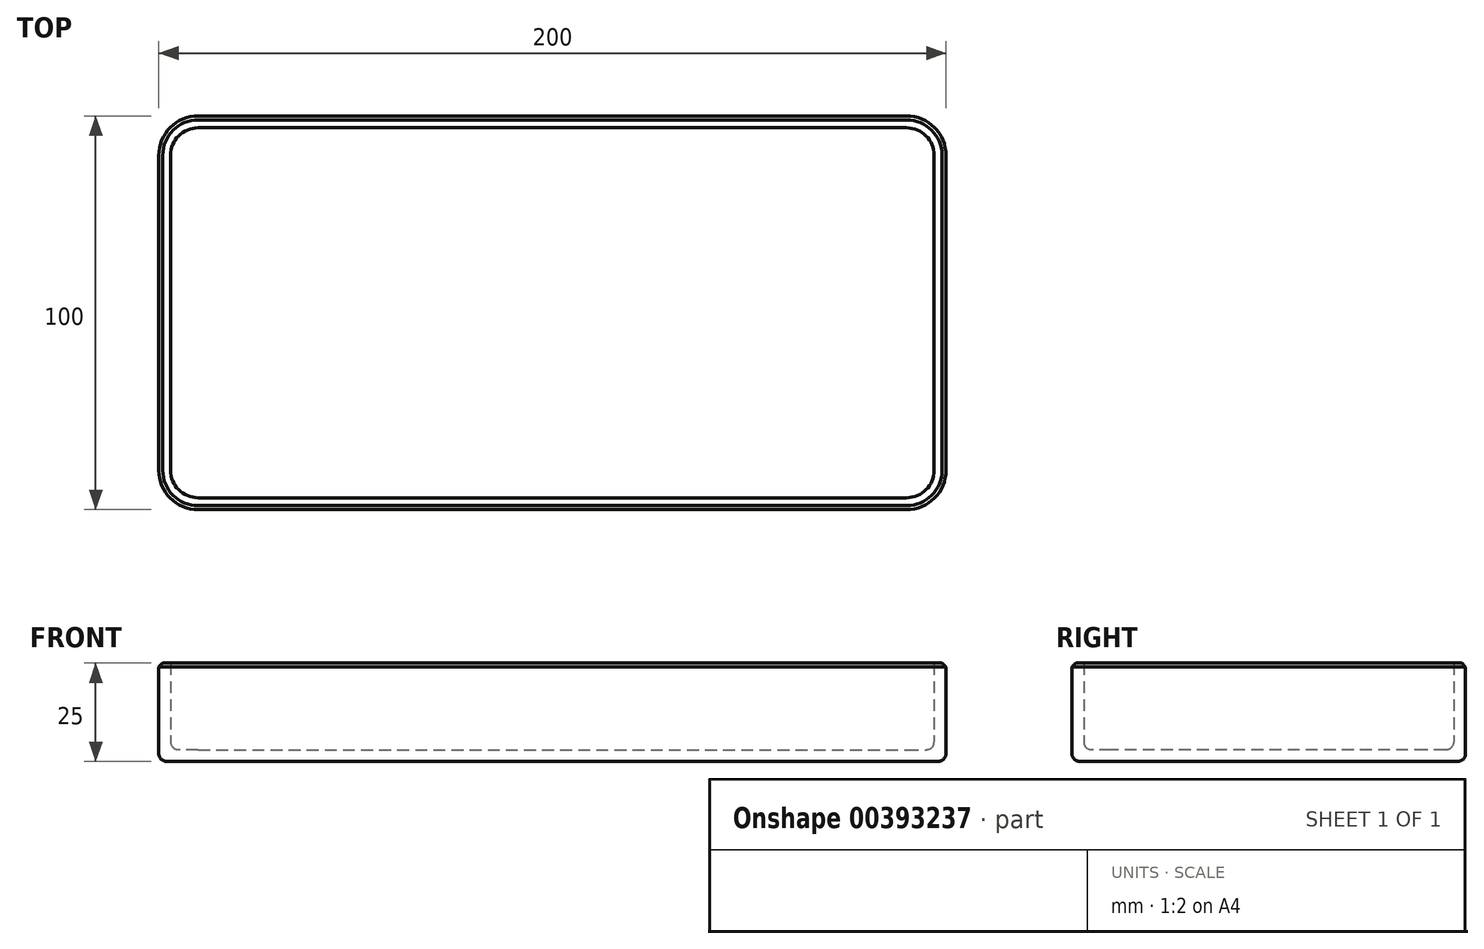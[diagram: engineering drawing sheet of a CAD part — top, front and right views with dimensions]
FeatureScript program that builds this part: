
annotation { "Feature Type Name" : "Feature", "Feature Type Description" : "" }
export const myFeature = defineFeature(function(context is Context, id is Id, definition is map)
    precondition{}
    {
        {
            var Q0;
            Q0=qCreatedBy(makeId("Top.planeOp"),FACE);
            var sketch = newSketch(context, id + "F0", { "sketchPlane" : qUnion([Q0])});
            skLineSegment(sketch, "E0.bottom", {"start": v(0.74, 0) * mm, "end": v(180.74, 0) * mm});
            skLineSegment(sketch, "E0.top", {"start": v(0.74, -100) * mm, "end": v(180.74, -100) * mm});
            skLineSegment(sketch, "E0.left", {"start": v(-9.26, -10) * mm, "end": v(-9.26, -90) * mm});
            skLineSegment(sketch, "E0.right", {"start": v(190.74, -10) * mm, "end": v(190.74, -90) * mm});
            skPoint(sketch, "E0.middle", {"position": v(90.74, -50) * mm});
            skPoint(sketch, "E1.visualSharp", {"position": v(-9.26, 0) * mm});
            skArc(sketch, "E1.filletArc", {"start": v(0.74, 0) * mm, "mid": v(-6.33, -2.93) * mm, "end": v(-9.26, -10) * mm});
            skPoint(sketch, "E2.visualSharp", {"position": v(-9.26, -100) * mm});
            skArc(sketch, "E2.filletArc", {"start": v(-9.26, -90) * mm, "mid": v(-6.33, -97.07) * mm, "end": v(0.74, -100) * mm});
            skPoint(sketch, "E3.visualSharp", {"position": v(190.74, -100) * mm});
            skArc(sketch, "E3.filletArc", {"start": v(180.74, -100) * mm, "mid": v(187.8, -97.07) * mm, "end": v(190.74, -90) * mm});
            skPoint(sketch, "E4.visualSharp", {"position": v(190.74, 0) * mm});
            skArc(sketch, "E4.filletArc", {"start": v(190.74, -10) * mm, "mid": v(187.8, -2.93) * mm, "end": v(180.74, 0) * mm});
            skLineSegment(sketch, "E5.0", {"start": v(0.74, -3) * mm, "end": v(180.74, -3) * mm});
            skArc(sketch, "E5.1", {"start": v(187.74, -10) * mm, "mid": v(185.69, -5.05) * mm, "end": v(180.74, -3) * mm});
            skArc(sketch, "E5.2", {"start": v(0.74, -3) * mm, "mid": v(-4.21, -5.05) * mm, "end": v(-6.26, -10) * mm});
            skLineSegment(sketch, "E5.3", {"start": v(187.74, -10) * mm, "end": v(187.74, -90) * mm});
            skLineSegment(sketch, "E5.4", {"start": v(-6.26, -10) * mm, "end": v(-6.26, -90) * mm});
            skArc(sketch, "E5.5", {"start": v(-6.26, -90) * mm, "mid": v(-4.21, -94.95) * mm, "end": v(0.74, -97) * mm});
            skLineSegment(sketch, "E5.6", {"start": v(0.74, -97) * mm, "end": v(180.74, -97) * mm});
            skArc(sketch, "E5.7", {"start": v(180.74, -97) * mm, "mid": v(185.69, -94.95) * mm, "end": v(187.74, -90) * mm});
            skSolve(sketch);
        }
        {
            var Q0;
            Q0=makeQuery(id+"F0.imprint","IMPRINT",FACE,{"disambiguationData":[TD([[makeQuery(id+"F0.imprint","IMPRINT",EDGE,{"derivedFrom":sQuery(id+"F0.wireOp",EDGE,"E0.bottom")}),-1.0]])]});
            extrude(context, id + "F1", {"entities" : qUnion([Q0]), "depth" : 25 * mm});
        }
        {
            var Q0;
            Q0=makeQuery(id+"F0.imprint","IMPRINT",FACE,{"disambiguationData":[TD([[makeQuery(id+"F0.imprint","IMPRINT",EDGE,{"derivedFrom":sQuery(id+"F0.wireOp",EDGE,"E5.0")}),-1.0]])]});
            extrude(context, id + "F2", {"entities" : qUnion([Q0]), "operationType" : NewBodyOperationType.ADD, "depth" : 3 * mm});
        }
        {
            var Q0;
            Q0=makeQuery(id+"F2.opExtrude","CAP_EDGE",EDGE,{"disambiguationData":[OSD([sQuery(id+"F0.wireOp",EDGE,"E5.4")])],"isStart":false});
            var Q1;
            Q1=makeQuery(id+"F2.opExtrude","CAP_EDGE",EDGE,{"disambiguationData":[OSD([sQuery(id+"F0.wireOp",EDGE,"E5.2")])],"isStart":false});
            var Q2;
            Q2=makeQuery(id+"F2.opExtrude","CAP_EDGE",EDGE,{"disambiguationData":[OSD([sQuery(id+"F0.wireOp",EDGE,"E5.0")])],"isStart":false});
            var Q3;
            Q3=makeQuery(id+"F2.opExtrude","CAP_FACE",FACE,{"disambiguationData":[OSD([sQuery(id+"F0.wireOp",EDGE,"E5.0"),sQuery(id+"F0.wireOp",EDGE,"E5.1"),sQuery(id+"F0.wireOp",EDGE,"E5.2"),sQuery(id+"F0.wireOp",EDGE,"E5.3"),sQuery(id+"F0.wireOp",EDGE,"E5.4"),sQuery(id+"F0.wireOp",EDGE,"E5.5"),sQuery(id+"F0.wireOp",EDGE,"E5.6"),sQuery(id+"F0.wireOp",EDGE,"E5.7")])],"isStart":false});
            fillet(context, id + "F3", {"entities" : qUnion([Q0, Q1, Q2, Q3]), "radius" : 2 * mm, "tangentPropagation" : true, "allowEdgeOverflow" : false});
        }
        {
            var Q0;
            Q0=makeQuery(id+"F1.opExtrude","CAP_EDGE",EDGE,{"disambiguationData":[OSD([sQuery(id+"F0.wireOp",EDGE,"E0.top")])],"isStart":true});
            var Q1;
            {var subQ0=sQuery(id+"F0.wireOp",EDGE,"E5.7");var subQ1=sQuery(id+"F0.wireOp",EDGE,"E5.6");var subQ2=sQuery(id+"F0.wireOp",EDGE,"E5.5");var subQ3=sQuery(id+"F0.wireOp",EDGE,"E5.4");var subQ4=sQuery(id+"F0.wireOp",EDGE,"E5.3");var subQ5=sQuery(id+"F0.wireOp",EDGE,"E5.2");var subQ6=sQuery(id+"F0.wireOp",EDGE,"E5.1");var subQ7=sQuery(id+"F0.wireOp",EDGE,"E5.0");Q1=makeQuery(id+"F2.boolean.opBoolean","MERGE",FACE,{"derivedFrom":[makeQuery(id+"F1.opExtrude","CAP_FACE",FACE,{"disambiguationData":[OSD([sQuery(id+"F0.wireOp",EDGE,"E0.bottom"),sQuery(id+"F0.wireOp",EDGE,"E0.top"),sQuery(id+"F0.wireOp",EDGE,"E0.left"),sQuery(id+"F0.wireOp",EDGE,"E0.right"),sQuery(id+"F0.wireOp",EDGE,"E1.filletArc"),sQuery(id+"F0.wireOp",EDGE,"E2.filletArc"),sQuery(id+"F0.wireOp",EDGE,"E3.filletArc"),sQuery(id+"F0.wireOp",EDGE,"E4.filletArc"),subQ7,subQ6,subQ5,subQ4,subQ3,subQ2,subQ1,subQ0])],"isStart":true}),makeQuery(id+"F2.opExtrude","CAP_FACE",FACE,{"disambiguationData":[OSD([subQ7,subQ6,subQ5,subQ4,subQ3,subQ2,subQ1,subQ0])],"isStart":true})]});}
            fillet(context, id + "F4", {"entities" : qUnion([Q0, Q1]), "radius" : 2 * mm, "tangentPropagation" : true, "allowEdgeOverflow" : false});
        }
        {
            var Q0;
            Q0=makeQuery(id+"F1.opExtrude","CAP_EDGE",EDGE,{"disambiguationData":[OSD([sQuery(id+"F0.wireOp",EDGE,"E0.left")])],"isStart":false});
            var Q1;
            Q1=makeQuery(id+"F1.opExtrude","CAP_EDGE",EDGE,{"disambiguationData":[OSD([sQuery(id+"F0.wireOp",EDGE,"E2.filletArc")])],"isStart":false});
            var Q2;
            Q2=makeQuery(id+"F1.opExtrude","CAP_EDGE",EDGE,{"disambiguationData":[OSD([sQuery(id+"F0.wireOp",EDGE,"E0.top")])],"isStart":false});
            var Q3;
            Q3=makeQuery(id+"F1.opExtrude","CAP_EDGE",EDGE,{"disambiguationData":[OSD([sQuery(id+"F0.wireOp",EDGE,"E3.filletArc")])],"isStart":false});
            var Q4;
            Q4=makeQuery(id+"F1.opExtrude","CAP_EDGE",EDGE,{"disambiguationData":[OSD([sQuery(id+"F0.wireOp",EDGE,"E0.right")])],"isStart":false});
            var Q5;
            Q5=makeQuery(id+"F1.opExtrude","CAP_EDGE",EDGE,{"disambiguationData":[OSD([sQuery(id+"F0.wireOp",EDGE,"E4.filletArc")])],"isStart":false});
            var Q6;
            Q6=makeQuery(id+"F1.opExtrude","CAP_EDGE",EDGE,{"disambiguationData":[OSD([sQuery(id+"F0.wireOp",EDGE,"E0.bottom")])],"isStart":false});
            chamfer(context, id + "F5", {"entities" : qUnion([Q0, Q1, Q2, Q3, Q4, Q5, Q6]), "width" : 1 * mm, "tangentPropagation" : true});
        }
    });
